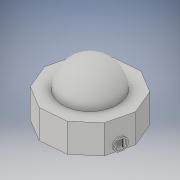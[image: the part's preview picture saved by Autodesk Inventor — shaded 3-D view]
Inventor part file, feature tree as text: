
AUTODESK INVENTOR PART (.ipt)
format: ipt  version: 2017 (Build 210142000, 142)  size: 257,536 bytes
history: native  units: in
note: dims shown in document units (in); Inventor stores cm internally (conversion verified against a paired STEP export)
features: other x8, sketch x7, extrude x6, mirror x1
ambient origin geometry x8: Origin, YZ Plane, XZ Plane, XY Plane, X Axis, Y Axis, Z Axis, Center Point
bodies: Solid1 (feature_tree)
feature tree (22):
  other  "dome"
  extrude  "bace"  Depth=1.0in TaperAngle=0.0deg
  extrude  "bace wall"  Depth=20.0in TaperAngle=0.0deg
  extrude  "bace cieiling"  Depth=6.6667in
  other  "dome work plane"
  extrude  "door frame"  Depth=1.0in TaperAngle=0.0deg
  extrude  "corridor connection"  Depth=0.25in
  extrude  "left door slot"  Depth=2.0in
  other  "door slot mirror"
  mirror  "Mirror1"
  other  "terminal connection parrale to door workplane"
  other  "left of door"
  other  "left 2 door"
  other  "right of door"
  other  "right 2 door"
  sketch  "Sketch1"  dims[d0=62.0in d1=1.0in d2=0.0in]
  sketch  "Sketch2"  dims[d4=1.0in d5=20.0in d6=0.0in]
  sketch  "Sketch3"  dims[d8=1.0in d9=0.0in d14=6.6667in d15=4.0in]
  sketch  "Sketch7"  dims[d16=2.0in d17=6.6667in d18=1.0in d19=0.0in]
  sketch  "Sketch8"  dims[d20=1.0in d21=0.0in d22=0.25in d23=0.5in d24=6.6667in]
  sketch  "Sketch9"  dims[d25=2.0in d26=0.0in d28=40.0in]
  sketch  "Sketch10"  dims[d32=20.0in d33=21.0in d34=90.0deg]
